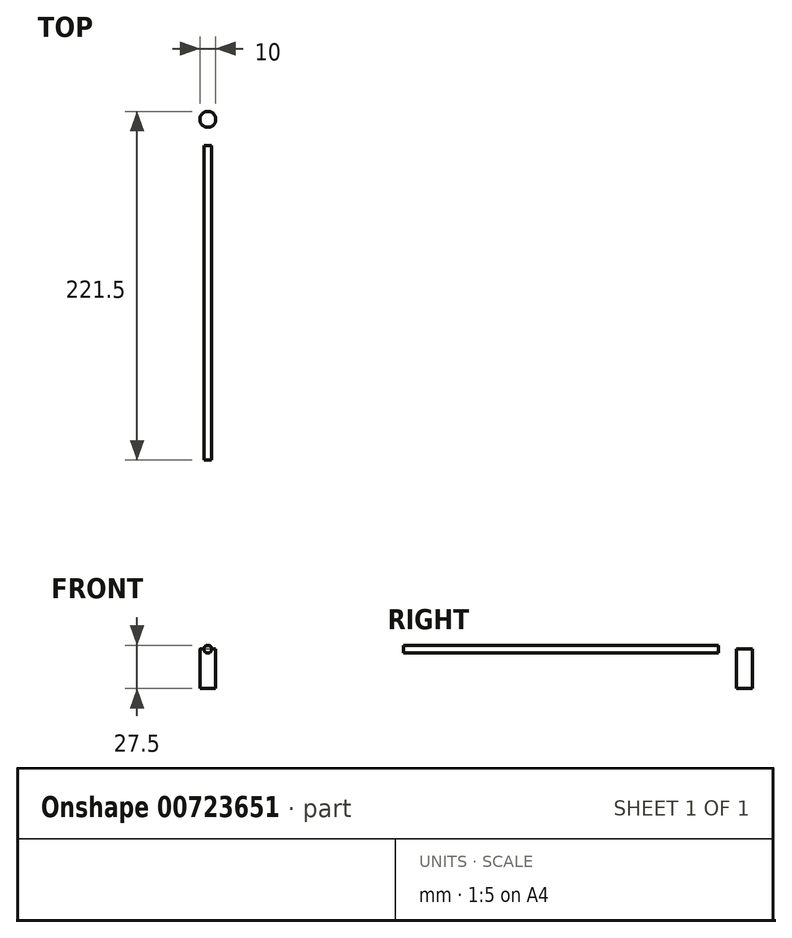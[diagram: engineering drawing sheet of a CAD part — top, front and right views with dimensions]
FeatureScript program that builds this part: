
annotation { "Feature Type Name" : "Feature", "Feature Type Description" : "" }
export const myFeature = defineFeature(function(context is Context, id is Id, definition is map)
    precondition{}
    {
        {
            var Q0;
            Q0=qCreatedBy(makeId("Front.planeOp"),FACE);
            var sketch = newSketch(context, id + "F0", { "sketchPlane" : qUnion([Q0])});
            skCircle(sketch, "E0", {"center": v(0, 0) * mm, "radius": 2.5 * mm});
            skSolve(sketch);
        }
        {
            var Q0;
            Q0=makeQuery(id+"F0.imprint","IMPRINT",FACE,{"disambiguationData":[TD([[makeQuery(id+"F0.imprint","IMPRINT",EDGE,{"derivedFrom":sQuery(id+"F0.wireOp",EDGE,"E0")}),1.0]])]});
            extrude(context, id + "F1", {"entities" : qUnion([Q0]), "depth" : 200 * mm, "offsetDistance" : 25 * mm});
        }
        {
            var Q0;
            Q0=qCreatedBy(makeId("Top.planeOp"),FACE);
            var sketch = newSketch(context, id + "F2", { "sketchPlane" : qUnion([Q0])});
            skCircle(sketch, "E1", {"center": v(0, 16.5) * mm, "radius": 5 * mm});
            skSolve(sketch);
        }
        {
            var Q0;
            Q0=makeQuery(id+"F2.imprint","IMPRINT",FACE,{"disambiguationData":[TD([[makeQuery(id+"F2.imprint","IMPRINT",EDGE,{"derivedFrom":sQuery(id+"F2.wireOp",EDGE,"E1")}),1.0]])]});
            extrude(context, id + "F3", {"entities" : qUnion([Q0]), "oppositeDirection" : true, "depth" : 25 * mm, "offsetDistance" : 25 * mm});
        }
    });
